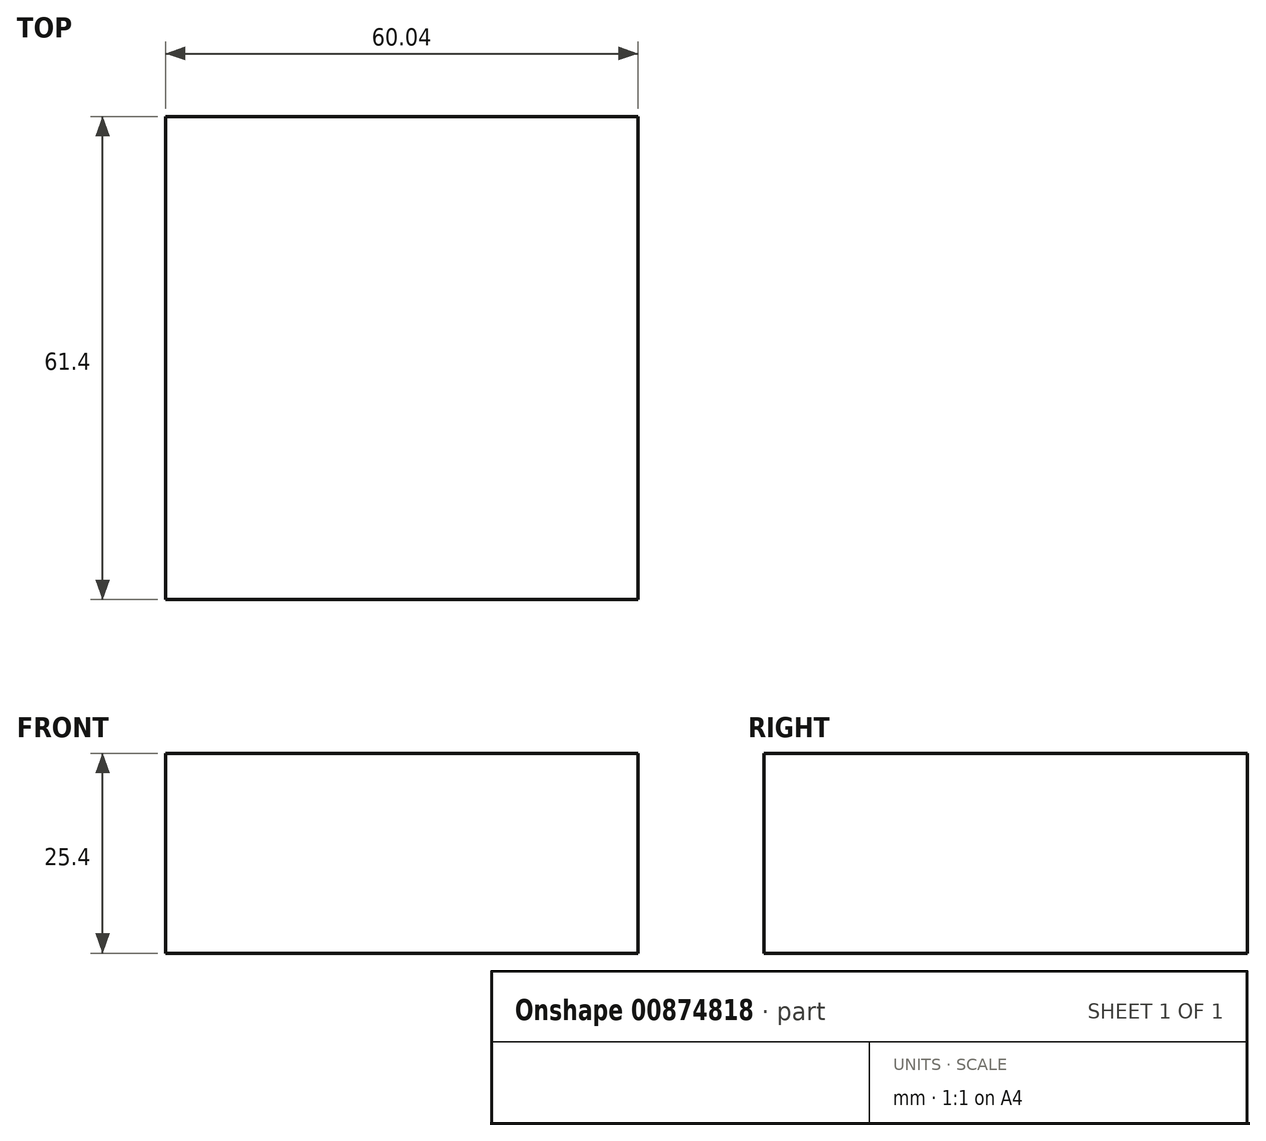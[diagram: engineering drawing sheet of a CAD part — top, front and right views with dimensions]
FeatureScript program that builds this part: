
annotation { "Feature Type Name" : "Feature", "Feature Type Description" : "" }
export const myFeature = defineFeature(function(context is Context, id is Id, definition is map)
    precondition{}
    {
        {
            var Q0;
            Q0=qCreatedBy(makeId("Top.planeOp"),FACE);
            var sketch = newSketch(context, id + "F0", { "sketchPlane" : qUnion([Q0])});
            skLineSegment(sketch, "E0.bottom", {"start": v(0, 0) * mm, "end": v(60.04, 0) * mm});
            skLineSegment(sketch, "E0.top", {"start": v(0, -61.4) * mm, "end": v(60.04, -61.4) * mm});
            skLineSegment(sketch, "E0.left", {"start": v(0, 0) * mm, "end": v(0, -61.4) * mm});
            skLineSegment(sketch, "E0.right", {"start": v(60.04, 0) * mm, "end": v(60.04, -61.4) * mm});
            skSolve(sketch);
        }
        {
            var Q0;
            Q0=makeQuery(id+"F0.imprint","IMPRINT",FACE,{"disambiguationData":[TD([[makeQuery(id+"F0.imprint","IMPRINT",EDGE,{"derivedFrom":sQuery(id+"F0.wireOp",EDGE,"E0.bottom")}),-1.0]])]});
            extrude(context, id + "F1", {"entities" : qUnion([Q0]), "oppositeDirection" : true, "depth" : 25.4 * mm});
        }
    });
